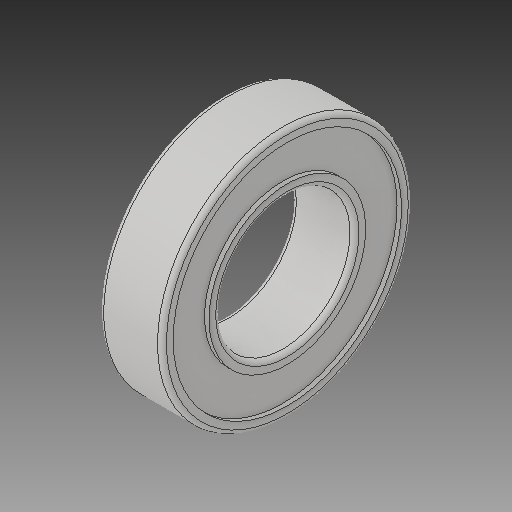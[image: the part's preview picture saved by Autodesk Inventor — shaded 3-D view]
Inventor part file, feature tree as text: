
AUTODESK INVENTOR PART (.ipt)
format: ipt  version: 2018 (Build 220112000, 112)  size: 176,640 bytes
history: native  units: in
note: dims shown in document units (in); Inventor stores cm internally (conversion verified against a paired STEP export)
features: fillet x1
ambient origin geometry x8: Origin, YZ Plane, XZ Plane, XY Plane, X Axis, Y Axis, Z Axis, Center Point
bodies: Solid1 (feature_tree)
feature tree (1):
  fillet  "Fillet1"  [1 undecoded]
note: 1 required parameter value undecoded (feature->parameter linkage not recoverable at this tier; creation-order binding heuristic only, values carry confidence <= 0.55)
